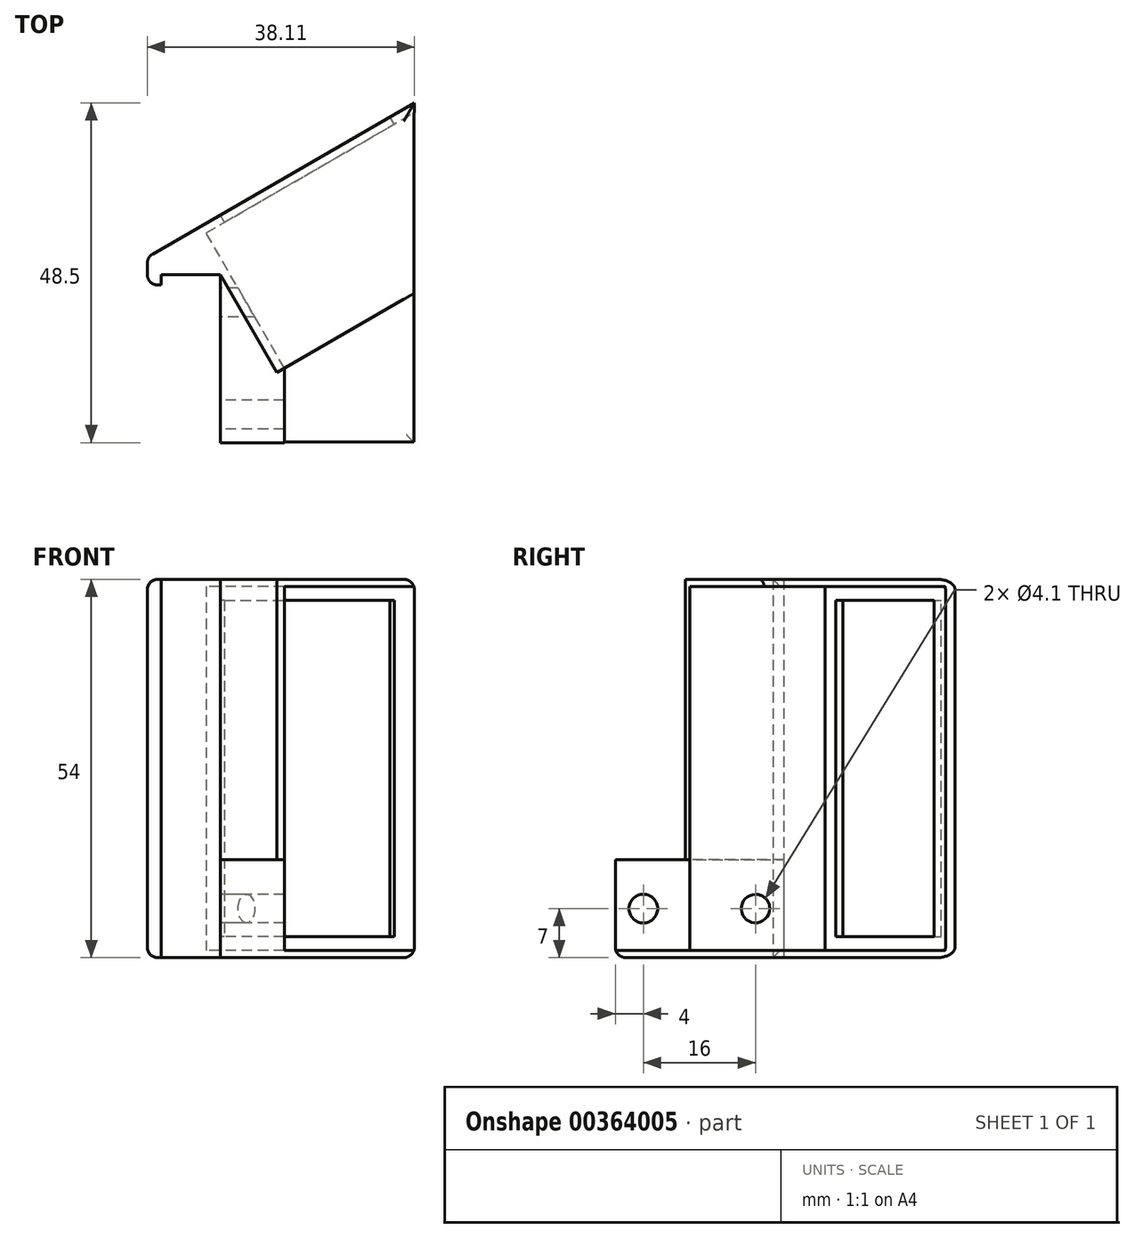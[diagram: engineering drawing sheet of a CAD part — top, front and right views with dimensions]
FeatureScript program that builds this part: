
annotation { "Feature Type Name" : "Feature", "Feature Type Description" : "" }
export const myFeature = defineFeature(function(context is Context, id is Id, definition is map)
    precondition{}
    {
        {
            var Q0;
            Q0=qCreatedBy(makeId("Top.planeOp"),FACE);
            var sketch = newSketch(context, id + "F0", { "sketchPlane" : qUnion([Q0])});
            skLineSegment(sketch, "E0", {"start": v(0, 0) * mm, "end": v(0, -1.5) * mm});
            skLineSegment(sketch, "E1", {"start": v(0, -1.5) * mm, "end": v(-2, -1.5) * mm});
            skLineSegment(sketch, "E2", {"start": v(-2, -1.5) * mm, "end": v(-2, 2.5) * mm});
            skLineSegment(sketch, "E3", {"start": v(36.11, 24.5) * mm, "end": v(36.11, -24) * mm});
            skLineSegment(sketch, "E4", {"start": v(36.11, -24) * mm, "end": v(8.4, -24) * mm});
            skLineSegment(sketch, "E5", {"start": v(8.4, -24) * mm, "end": v(8.4, 0) * mm});
            skLineSegment(sketch, "E6", {"start": v(8.4, 0) * mm, "end": v(0, 0) * mm});
            skLineSegment(sketch, "E7", {"start": v(-2, 2.5) * mm, "end": v(8.4, 8.5) * mm});
            skLineSegment(sketch, "E8", {"start": v(8.4, 8.5) * mm, "end": v(36.11, 24.5) * mm});
            skSolve(sketch);
        }
        {
            var Q0;
            Q0 = qSketchRegion(id + "F0", true);
            extrude(context, id + "F1", {"entities" : qUnion([Q0]), "depth" : 54 * mm, "offsetDistance" : 25 * mm});
        }
        {
            var Q0;
            Q0=makeQuery(id+"F1.opExtrude","SWEPT_FACE",FACE,{"disambiguationData":[OSD([sQuery(id+"F0.wireOp",EDGE,"E7"),sQuery(id+"F0.wireOp",EDGE,"E8")])]});
            var sketch = newSketch(context, id + "F2", { "sketchPlane" : qUnion([Q0])});
            skLineSegment(sketch, "E9.bottom", {"start": v(-11.53, 3) * mm, "end": v(-39.53, 3) * mm});
            skLineSegment(sketch, "E9.top", {"start": v(-11.53, 51) * mm, "end": v(-39.53, 51) * mm});
            skLineSegment(sketch, "E9.left", {"start": v(-11.53, 3) * mm, "end": v(-11.53, 51) * mm});
            skLineSegment(sketch, "E9.right", {"start": v(-39.53, 3) * mm, "end": v(-39.53, 51) * mm});
            skPoint(sketch, "E9.middle", {"position": v(-25.53, 27) * mm});
            skPoint(sketch, "E9.middle.positionSnap0", {"position": v(-43.53, 27) * mm});
            skPoint(sketch, "E9.centerSnap0", {"position": v(-43.53, 27) * mm});
            skSolve(sketch);
        }
        {
            var Q0;
            Q0 = qSketchRegion(id + "F2", true);
            extrude(context, id + "F3", {"entities" : qUnion([Q0]), "operationType" : NewBodyOperationType.REMOVE, "oppositeDirection" : true, "depth" : 50 * mm, "offsetDistance" : 25 * mm});
        }
        {
            var Q0;
            Q0=makeQuery(id+"F3.boolean.opBoolean","COPY",FACE,{"derivedFrom":makeQuery(id+"F3.opExtrude","SWEPT_FACE",FACE,{"disambiguationData":[OSD([sQuery(id+"F2.wireOp",EDGE,"E9.left")])]})});
            var sketch = newSketch(context, id + "F4", { "sketchPlane" : qUnion([Q0])});
            skLineSegment(sketch, "E10.bottom", {"start": v(-34.37, 51) * mm, "end": v(1.97, 51) * mm});
            skLineSegment(sketch, "E10.top", {"start": v(-34.37, 3) * mm, "end": v(1.97, 3) * mm});
            skLineSegment(sketch, "E10.left", {"start": v(-34.37, 51) * mm, "end": v(-34.37, 3) * mm});
            skLineSegment(sketch, "E10.right", {"start": v(1.97, 51) * mm, "end": v(1.97, 3) * mm});
            skSolve(sketch);
        }
        {
            var Q0;
            Q0 = qSketchRegion(id + "F4", true);
            extrude(context, id + "F5", {"entities" : qUnion([Q0]), "operationType" : NewBodyOperationType.REMOVE, "oppositeDirection" : true, "depth" : 3 * mm, "offsetDistance" : 25 * mm});
        }
        {
            var Q0;
            Q0=makeQuery(id+"F3.boolean.opBoolean","COPY",FACE,{"derivedFrom":makeQuery(id+"F3.opExtrude","SWEPT_FACE",FACE,{"disambiguationData":[OSD([sQuery(id+"F2.wireOp",EDGE,"E9.right")])]})});
            var sketch = newSketch(context, id + "F6", { "sketchPlane" : qUnion([Q0])});
            skLineSegment(sketch, "E11.bottom", {"start": v(3.76, 51) * mm, "end": v(-1.97, 51) * mm});
            skLineSegment(sketch, "E11.top", {"start": v(3.76, 3) * mm, "end": v(-1.97, 3) * mm});
            skLineSegment(sketch, "E11.left", {"start": v(3.76, 51) * mm, "end": v(3.76, 3) * mm});
            skLineSegment(sketch, "E11.right", {"start": v(-1.97, 51) * mm, "end": v(-1.97, 3) * mm});
            skSolve(sketch);
        }
        {
            var Q0;
            Q0 = qSketchRegion(id + "F6", true);
            extrude(context, id + "F7", {"entities" : qUnion([Q0]), "operationType" : NewBodyOperationType.REMOVE, "oppositeDirection" : true, "depth" : 20 * mm, "offsetDistance" : 25 * mm});
        }
        {
            var Q0;
            Q0=makeQuery(id+"F7.boolean.opBoolean","MERGE",FACE,{"derivedFrom":[makeQuery(id+"F5.boolean.opBoolean","MERGE",FACE,{"derivedFrom":[makeQuery(id+"F3.boolean.opBoolean","COPY",FACE,{"derivedFrom":makeQuery(id+"F3.opExtrude","SWEPT_FACE",FACE,{"disambiguationData":[OSD([sQuery(id+"F2.wireOp",EDGE,"E9.top")])]})}),makeQuery(id+"F5.opExtrude","SWEPT_FACE",FACE,{"disambiguationData":[OSD([sQuery(id+"F4.wireOp",EDGE,"E10.bottom")])]})]}),makeQuery(id+"F7.opExtrude","SWEPT_FACE",FACE,{"disambiguationData":[OSD([sQuery(id+"F6.wireOp",EDGE,"E11.bottom")])]})]});
            var sketch = newSketch(context, id + "F8", { "sketchPlane" : qUnion([Q0])});
            skLineSegment(sketch, "E12", {"start": v(36.11, 24) * mm, "end": v(23.7, 24) * mm});
            skLineSegment(sketch, "E13", {"start": v(23.7, 24) * mm, "end": v(6.4, -5.97) * mm});
            skLineSegment(sketch, "E14", {"start": v(6.4, -5.97) * mm, "end": v(36.11, -23.12) * mm});
            skLineSegment(sketch, "E15", {"start": v(36.11, -23.12) * mm, "end": v(36.11, 24) * mm});
            skSolve(sketch);
        }
        {
            var Q0;
            Q0 = qSketchRegion(id + "F8", true);
            extrude(context, id + "F9", {"entities" : qUnion([Q0]), "operationType" : NewBodyOperationType.REMOVE, "oppositeDirection" : true, "depth" : 2 * mm, "offsetDistance" : 25 * mm});
        }
        {
            var Q0;
            Q0=makeQuery(id+"F7.boolean.opBoolean","MERGE",FACE,{"derivedFrom":[makeQuery(id+"F5.boolean.opBoolean","MERGE",FACE,{"derivedFrom":[makeQuery(id+"F3.boolean.opBoolean","COPY",FACE,{"derivedFrom":makeQuery(id+"F3.opExtrude","SWEPT_FACE",FACE,{"disambiguationData":[OSD([sQuery(id+"F2.wireOp",EDGE,"E9.bottom")])]})}),makeQuery(id+"F5.opExtrude","SWEPT_FACE",FACE,{"disambiguationData":[OSD([sQuery(id+"F4.wireOp",EDGE,"E10.top")])]})]}),makeQuery(id+"F7.opExtrude","SWEPT_FACE",FACE,{"disambiguationData":[OSD([sQuery(id+"F6.wireOp",EDGE,"E11.top")])]})]});
            var sketch = newSketch(context, id + "F10", { "sketchPlane" : qUnion([Q0])});
            skLineSegment(sketch, "E16", {"start": v(6.4, 5.97) * mm, "end": v(23.7, -24) * mm});
            skLineSegment(sketch, "E17", {"start": v(23.7, -24) * mm, "end": v(36.11, -24) * mm});
            skLineSegment(sketch, "E18", {"start": v(36.11, -24) * mm, "end": v(36.11, 23.12) * mm});
            skLineSegment(sketch, "E19", {"start": v(36.11, 23.12) * mm, "end": v(6.4, 5.97) * mm});
            skSolve(sketch);
        }
        {
            var Q0;
            Q0 = qSketchRegion(id + "F10", true);
            extrude(context, id + "F11", {"entities" : qUnion([Q0]), "operationType" : NewBodyOperationType.REMOVE, "oppositeDirection" : true, "depth" : 2 * mm, "offsetDistance" : 25 * mm});
        }
        {
            var Q0;
            Q0=makeQuery(id+"F1.opExtrude","CAP_FACE",FACE,{"disambiguationData":[OSD([sQuery(id+"F0.wireOp",EDGE,"E0"),sQuery(id+"F0.wireOp",EDGE,"E1"),sQuery(id+"F0.wireOp",EDGE,"E2"),sQuery(id+"F0.wireOp",EDGE,"E3"),sQuery(id+"F0.wireOp",EDGE,"E4"),sQuery(id+"F0.wireOp",EDGE,"E5"),sQuery(id+"F0.wireOp",EDGE,"E6"),sQuery(id+"F0.wireOp",EDGE,"E7"),sQuery(id+"F0.wireOp",EDGE,"E8")])],"isStart":false});
            var sketch = newSketch(context, id + "F12", { "sketchPlane" : qUnion([Q0])});
            skLineSegment(sketch, "E20", {"start": v(8.4, 0) * mm, "end": v(16.48, -14) * mm});
            skLineSegment(sketch, "E21", {"start": v(8.4, -24) * mm, "end": v(8.4, 0) * mm});
            skLineSegment(sketch, "E22", {"start": v(16.48, -14) * mm, "end": v(36.11, -2.67) * mm});
            skLineSegment(sketch, "E23", {"start": v(36.11, -2.67) * mm, "end": v(36.11, -24) * mm});
            skLineSegment(sketch, "E24", {"start": v(36.11, -24) * mm, "end": v(8.4, -24) * mm});
            skSolve(sketch);
        }
        {
            var Q0;
            Q0 = qSketchRegion(id + "F12", true);
            extrude(context, id + "F13", {"entities" : qUnion([Q0]), "operationType" : NewBodyOperationType.REMOVE, "oppositeDirection" : true, "depth" : 40 * mm, "offsetDistance" : 25 * mm});
        }
        {
            var Q0;
            Q0=makeQuery(id+"F13.boolean.opBoolean","COPY",FACE,{"derivedFrom":makeQuery(id+"F13.opExtrude","CAP_FACE",FACE,{"disambiguationData":[OSD([sQuery(id+"F12.wireOp",EDGE,"E20"),sQuery(id+"F12.wireOp",EDGE,"E21"),sQuery(id+"F12.wireOp",EDGE,"E22"),sQuery(id+"F12.wireOp",EDGE,"E23"),sQuery(id+"F12.wireOp",EDGE,"E24")])],"isStart":false})});
            var sketch = newSketch(context, id + "F14", { "sketchPlane" : qUnion([Q0])});
            skLineSegment(sketch, "E25", {"start": v(17.57, -13.37) * mm, "end": v(17.57, -24) * mm});
            skLineSegment(sketch, "E26", {"start": v(17.57, -24) * mm, "end": v(23.7, -24) * mm});
            skLineSegment(sketch, "E27", {"start": v(23.7, -24) * mm, "end": v(17.57, -13.37) * mm});
            skSolve(sketch);
        }
        {
            var Q0;
            Q0 = qSketchRegion(id + "F14", true);
            extrude(context, id + "F15", {"entities" : qUnion([Q0]), "operationType" : NewBodyOperationType.REMOVE, "oppositeDirection" : true, "depth" : 13 * mm, "offsetDistance" : 25 * mm});
        }
        {
            var Q0;
            Q0=makeQuery(id+"F1.opExtrude","SWEPT_FACE",FACE,{"disambiguationData":[OSD([sQuery(id+"F0.wireOp",EDGE,"E5")])]});
            var sketch = newSketch(context, id + "F16", { "sketchPlane" : qUnion([Q0])});
            skCircle(sketch, "E28", {"center": v(20, 7) * mm, "radius": 2.05 * mm});
            skPoint(sketch, "E28.centerSnap0", {"position": v(24, 7) * mm});
            skCircle(sketch, "E29", {"center": v(4, 7) * mm, "radius": 2.05 * mm});
            skSolve(sketch);
        }
        {
            var Q0;
            Q0 = qSketchRegion(id + "F16", true);
            extrude(context, id + "F17", {"entities" : qUnion([Q0]), "operationType" : NewBodyOperationType.REMOVE, "oppositeDirection" : true, "depth" : 25 * mm, "offsetDistance" : 25 * mm});
        }
        {
            var Q0;
            Q0=makeQuery(id+"F1.opExtrude","CAP_EDGE",EDGE,{"disambiguationData":[OSD([sQuery(id+"F0.wireOp",EDGE,"E7"),sQuery(id+"F0.wireOp",EDGE,"E8")])],"isStart":false});
            var Q1;
            Q1=makeQuery(id+"F1.opExtrude","SWEPT_EDGE",EDGE,{"disambiguationData":[OSD([sQuery(id+"F0.wireOp",EDGE,"E1"),sQuery(id+"F0.wireOp",EDGE,"E2")])]});
            var Q2;
            Q2=makeQuery(id+"F1.opExtrude","CAP_EDGE",EDGE,{"disambiguationData":[OSD([sQuery(id+"F0.wireOp",EDGE,"E2")])],"isStart":false});
            var Q3;
            Q3=makeQuery(id+"F1.opExtrude","CAP_EDGE",EDGE,{"disambiguationData":[OSD([sQuery(id+"F0.wireOp",EDGE,"E2")])],"isStart":true});
            var Q4;
            Q4=makeQuery(id+"F13.boolean.opBoolean","COPY",EDGE,{"derivedFrom":makeQuery(id+"F13.opExtrude","CAP_EDGE",EDGE,{"disambiguationData":[OSD([sQuery(id+"F12.wireOp",EDGE,"E22")])],"isStart":true})});
            var Q5;
            Q5=makeQuery(id+"F13.boolean.opBoolean","COPY",EDGE,{"derivedFrom":makeQuery(id+"F13.opExtrude","CAP_EDGE",EDGE,{"disambiguationData":[OSD([sQuery(id+"F12.wireOp",EDGE,"E20")])],"isStart":true})});
            var Q6;
            Q6=makeQuery(id+"F1.opExtrude","CAP_EDGE",EDGE,{"disambiguationData":[OSD([sQuery(id+"F0.wireOp",EDGE,"E3")])],"isStart":true});
            var Q7;
            Q7=makeQuery(id+"F1.opExtrude","CAP_EDGE",EDGE,{"disambiguationData":[OSD([sQuery(id+"F0.wireOp",EDGE,"E4")])],"isStart":true});
            var Q8;
            Q8=makeQuery(id+"F1.opExtrude","SWEPT_EDGE",EDGE,{"disambiguationData":[OSD([sQuery(id+"F0.wireOp",EDGE,"E2"),sQuery(id+"F0.wireOp",EDGE,"E7")])]});
            var Q9;
            Q9=makeQuery(id+"F13.boolean.opBoolean","COPY",EDGE,{"derivedFrom":makeQuery(id+"F13.opExtrude","CAP_EDGE",EDGE,{"disambiguationData":[OSD([sQuery(id+"F12.wireOp",EDGE,"E24")])],"isStart":false})});
            var Q10;
            Q10=makeQuery(id+"F1.opExtrude","CAP_EDGE",EDGE,{"disambiguationData":[OSD([sQuery(id+"F0.wireOp",EDGE,"E7"),sQuery(id+"F0.wireOp",EDGE,"E8")])],"isStart":true});
            var Q11;
            Q11=makeQuery(id+"F1.opExtrude","CAP_EDGE",EDGE,{"disambiguationData":[OSD([sQuery(id+"F0.wireOp",EDGE,"E3")])],"isStart":false});
            fillet(context, id + "F18", {"entities" : qUnion([Q0, Q1, Q2, Q3, Q4, Q5, Q6, Q7, Q8, Q9, Q10, Q11]), "radius" : 1.5 * mm, "tangentPropagation" : true, "allowEdgeOverflow" : false});
        }
    });
